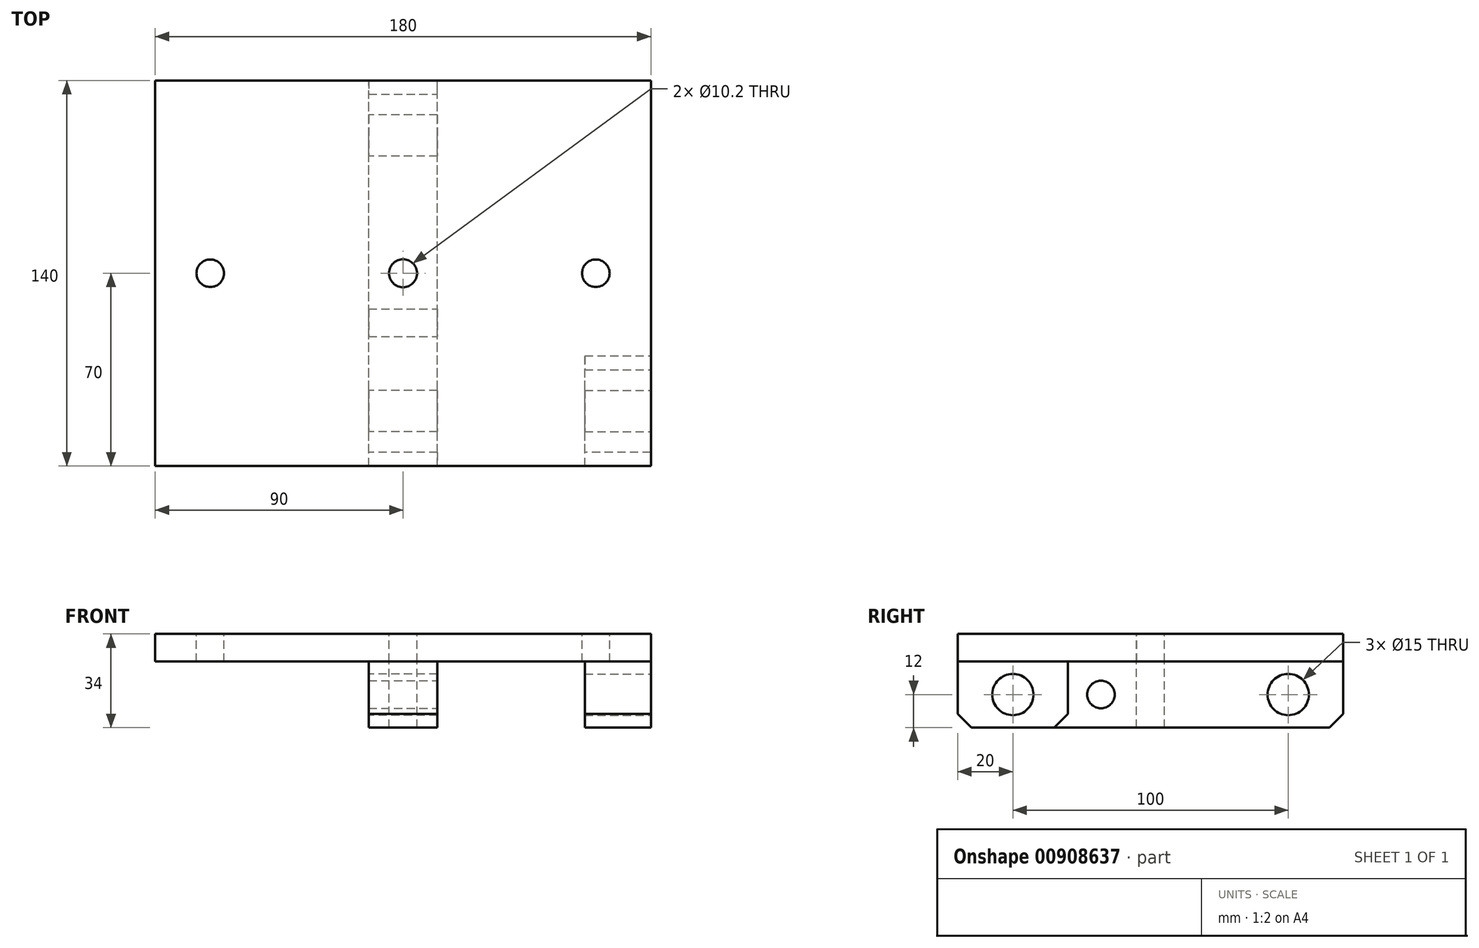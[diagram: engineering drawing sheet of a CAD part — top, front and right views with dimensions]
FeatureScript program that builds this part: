
annotation { "Feature Type Name" : "Feature", "Feature Type Description" : "" }
export const myFeature = defineFeature(function(context is Context, id is Id, definition is map)
    precondition{}
    {
        {
            var Q0;
            Q0=qCreatedBy(makeId("Right.planeOp"),FACE);
            var sketch = newSketch(context, id + "F0", { "sketchPlane" : qUnion([Q0])});
            skLineSegment(sketch, "E0.bottom", {"start": v(-70, -10) * mm, "end": v(70, -10) * mm});
            skLineSegment(sketch, "E0.top", {"start": v(-70, 0) * mm, "end": v(70, 0) * mm});
            skLineSegment(sketch, "E0.left", {"start": v(-70, -10) * mm, "end": v(-70, 0) * mm});
            skLineSegment(sketch, "E0.right", {"start": v(70, -10) * mm, "end": v(70, 0) * mm});
            skLineSegment(sketch, "E1.top", {"start": v(-70, -34) * mm, "end": v(70, -34) * mm});
            skLineSegment(sketch, "E1.left", {"start": v(-70, -10) * mm, "end": v(-70, -34) * mm});
            skLineSegment(sketch, "E1.right", {"start": v(70, -10) * mm, "end": v(70, -34) * mm});
            skCircle(sketch, "E2", {"center": v(-50, -22) * mm, "radius": 7.5 * mm});
            skLineSegment(sketch, "E3", {"start": v(-70, -22) * mm, "end": v(70, -22) * mm, "construction": true});
            skCircle(sketch, "E4", {"center": v(-50, -22) * mm, "radius": 6 * mm});
            skLineSegment(sketch, "E5", {"start": v(0, 0) * mm, "end": v(0, -34) * mm, "construction": true});
            skCircle(sketch, "E6.MirrorC", {"center": v(50, -22) * mm, "radius": 6 * mm});
            skCircle(sketch, "E7.MirrorC", {"center": v(50, -22) * mm, "radius": 7.5 * mm});
            skSolve(sketch);
        }
        {
            var Q0;
            Q0=makeQuery(id+"F0.imprint","IMPRINT",FACE,{"disambiguationData":[TD([[makeQuery(id+"F0.imprint","IMPRINT",EDGE,{"derivedFrom":sQuery(id+"F0.wireOp",EDGE,"E0.top")}),-1.0]])]});
            extrude(context, id + "F1", {"entities" : qUnion([Q0]), "endBound" : BoundingType.SYMMETRIC, "depth" : 180 * mm, "offsetDistance" : 25 * mm});
        }
        {
            var Q0;
            Q0=makeQuery(id+"F0.imprint","IMPRINT",FACE,{"disambiguationData":[TD([[makeQuery(id+"F0.imprint","IMPRINT",EDGE,{"derivedFrom":sQuery(id+"F0.wireOp",EDGE,"E0.bottom")}),-1.0]])]});
            extrude(context, id + "F2", {"entities" : qUnion([Q0]), "endBound" : BoundingType.SYMMETRIC, "depth" : 25 * mm, "offsetDistance" : 25 * mm});
        }
        {
            var Q0;
            Q0=makeQuery(id+"F1.opExtrude","SWEPT_FACE",FACE,{"disambiguationData":[OSD([sQuery(id+"F0.wireOp",EDGE,"E0.top")])]});
            var sketch = newSketch(context, id + "F3", { "sketchPlane" : qUnion([Q0])});
            skCircle(sketch, "E8", {"center": v(0, 0) * mm, "radius": 5.1 * mm});
            skSolve(sketch);
        }
        {
            var Q0;
            Q0 = qSketchRegion(id + "F3", true);
            var Q1;
            Q1=makeQuery(id+"F2.opExtrude","SWEPT_FACE",FACE,{"disambiguationData":[OSD([sQuery(id+"F0.wireOp",EDGE,"E1.top")])]});
            var Q2;
            Q2=makeQuery(id+"F2.opExtrude","SWEPT_FACE",FACE,{"disambiguationData":[OSD([sQuery(id+"F0.wireOp",EDGE,"E1.top")])]});
            extrude(context, id + "F4", {"entities" : qUnion([Q0, Q1]), "operationType" : NewBodyOperationType.REMOVE, "endBound" : BoundingType.THROUGH_ALL, "oppositeDirection" : true, "depth" : 25 * mm, "endBoundEntityFace" : qUnion([Q2]), "offsetDistance" : 25 * mm});
        }
        {
            var Q0;
            Q0=makeQuery(id+"F1.opExtrude","CAP_FACE",FACE,{"disambiguationData":[OSD([sQuery(id+"F0.wireOp",EDGE,"E0.top"),sQuery(id+"F0.wireOp",EDGE,"E0.left"),sQuery(id+"F0.wireOp",EDGE,"E0.right"),sQuery(id+"F0.wireOp",EDGE,"E0.bottom")])],"isStart":false});
            cPlane(context, id + "F5", {"entities" : qUnion([Q0]), "cplaneType" : CPlaneType.OFFSET, "offset" : 0 * mm, "width" : 150 * mm, "height" : 150 * mm});
        }
        {
            var Q0;
            Q0=qCreatedBy(id+"F5.planeOp",FACE);
            var sketch = newSketch(context, id + "F6", { "sketchPlane" : qUnion([Q0])});
            skLineSegment(sketch, "E9.bottom", {"start": v(-70, -10) * mm, "end": v(-30, -10) * mm});
            skLineSegment(sketch, "E9.top", {"start": v(-70, -34) * mm, "end": v(-30, -34) * mm});
            skLineSegment(sketch, "E9.left", {"start": v(-70, -10) * mm, "end": v(-70, -34) * mm});
            skLineSegment(sketch, "E9.right", {"start": v(-30, -10) * mm, "end": v(-30, -34) * mm});
            skPoint(sketch, "E10.0", {"position": v(-70, -10) * mm});
            skCircle(sketch, "E11.0", {"center": v(-50, -22) * mm, "radius": 6 * mm});
            skCircle(sketch, "E12.0", {"center": v(-50, -22) * mm, "radius": 7.5 * mm});
            skLineSegment(sketch, "E13", {"start": v(-50, -22) * mm, "end": v(-70, -22) * mm, "construction": true});
            skLineSegment(sketch, "E14", {"start": v(-50, -22) * mm, "end": v(-30, -22) * mm, "construction": true});
            skPoint(sketch, "E15.0", {"position": v(-70, -34) * mm});
            skSolve(sketch);
        }
        {
            var Q0;
            Q0 = qSketchRegion(id + "F6", true);
            extrude(context, id + "F7", {"entities" : qUnion([Q0]), "oppositeDirection" : true, "depth" : 24 * mm, "offsetDistance" : 25 * mm});
        }
        {
            var Q0;
            Q0=makeQuery(id+"F1.opExtrude","SWEPT_FACE",FACE,{"disambiguationData":[OSD([sQuery(id+"F0.wireOp",EDGE,"E0.top")])]});
            var sketch = newSketch(context, id + "F8", { "sketchPlane" : qUnion([Q0])});
            skCircle(sketch, "E16", {"center": v(0, 0) * mm, "radius": 5.1 * mm});
            skSolve(sketch);
        }
        {
            var Q0;
            Q0 = qSketchRegion(id + "F8", true);
            extrude(context, id + "F9", {"entities" : qUnion([Q0]), "operationType" : NewBodyOperationType.REMOVE, "endBound" : BoundingType.THROUGH_ALL, "oppositeDirection" : true, "depth" : 25 * mm, "offsetDistance" : 25 * mm});
        }
        {
            var Q0;
            Q0=makeQuery(id+"F1.opExtrude","SWEPT_FACE",FACE,{"disambiguationData":[OSD([sQuery(id+"F0.wireOp",EDGE,"E0.top")])]});
            var sketch = newSketch(context, id + "F10", { "sketchPlane" : qUnion([Q0])});
            skLineSegment(sketch, "E17", {"start": v(0, 0) * mm, "end": v(-70, 0) * mm, "construction": true});
            skCircle(sketch, "E18", {"center": v(-70, 0) * mm, "radius": 5 * mm});
            skLineSegment(sketch, "E19", {"start": v(0, 0) * mm, "end": v(70, 0) * mm, "construction": true});
            skCircle(sketch, "E20", {"center": v(70, 0) * mm, "radius": 5 * mm});
            skSolve(sketch);
        }
        {
            var Q0;
            Q0 = qSketchRegion(id + "F10", true);
            extrude(context, id + "F11", {"entities" : qUnion([Q0]), "operationType" : NewBodyOperationType.REMOVE, "endBound" : BoundingType.THROUGH_ALL, "oppositeDirection" : true, "depth" : 25 * mm, "offsetDistance" : 25 * mm});
        }
        {
            var Q0;
            Q0=makeQuery(id+"F7.opExtrude","SWEPT_EDGE",EDGE,{"disambiguationData":[OSD([sQuery(id+"F6.wireOp",EDGE,"E9.top"),sQuery(id+"F6.wireOp",EDGE,"E9.left")])]});
            var Q1;
            Q1=makeQuery(id+"F7.opExtrude","SWEPT_EDGE",EDGE,{"disambiguationData":[OSD([sQuery(id+"F6.wireOp",EDGE,"E9.top"),sQuery(id+"F6.wireOp",EDGE,"E9.right")])]});
            var Q2;
            Q2=makeQuery(id+"F2.opExtrude","SWEPT_EDGE",EDGE,{"disambiguationData":[OSD([sQuery(id+"F0.wireOp",EDGE,"E1.top"),sQuery(id+"F0.wireOp",EDGE,"E1.left")])]});
            var Q3;
            Q3=makeQuery(id+"F2.opExtrude","SWEPT_EDGE",EDGE,{"disambiguationData":[OSD([sQuery(id+"F0.wireOp",EDGE,"E1.top"),sQuery(id+"F0.wireOp",EDGE,"E1.right")])]});
            chamfer(context, id + "F12", {"entities" : qUnion([Q0, Q1, Q2, Q3]), "width" : 5 * mm, "tangentPropagation" : true});
        }
        {
            var Q0;
            Q0=makeQuery(id+"F2.opExtrude","CAP_FACE",FACE,{"disambiguationData":[OSD([sQuery(id+"F0.wireOp",EDGE,"E0.bottom"),sQuery(id+"F0.wireOp",EDGE,"E1.top"),sQuery(id+"F0.wireOp",EDGE,"E1.left"),sQuery(id+"F0.wireOp",EDGE,"E1.right"),sQuery(id+"F0.wireOp",EDGE,"E2"),sQuery(id+"F0.wireOp",EDGE,"E7.MirrorC")])],"isStart":false});
            var sketch = newSketch(context, id + "F13", { "sketchPlane" : qUnion([Q0])});
            skLineSegment(sketch, "E21", {"start": v(-18, -10) * mm, "end": v(-18, -34) * mm, "construction": true});
            skCircle(sketch, "E22", {"center": v(-18, -22) * mm, "radius": 5 * mm});
            skSolve(sketch);
        }
        {
            var Q0;
            Q0 = qSketchRegion(id + "F13", true);
            extrude(context, id + "F14", {"entities" : qUnion([Q0]), "operationType" : NewBodyOperationType.REMOVE, "endBound" : BoundingType.THROUGH_ALL, "oppositeDirection" : true, "depth" : 25 * mm, "offsetDistance" : 25 * mm});
        }
    });
